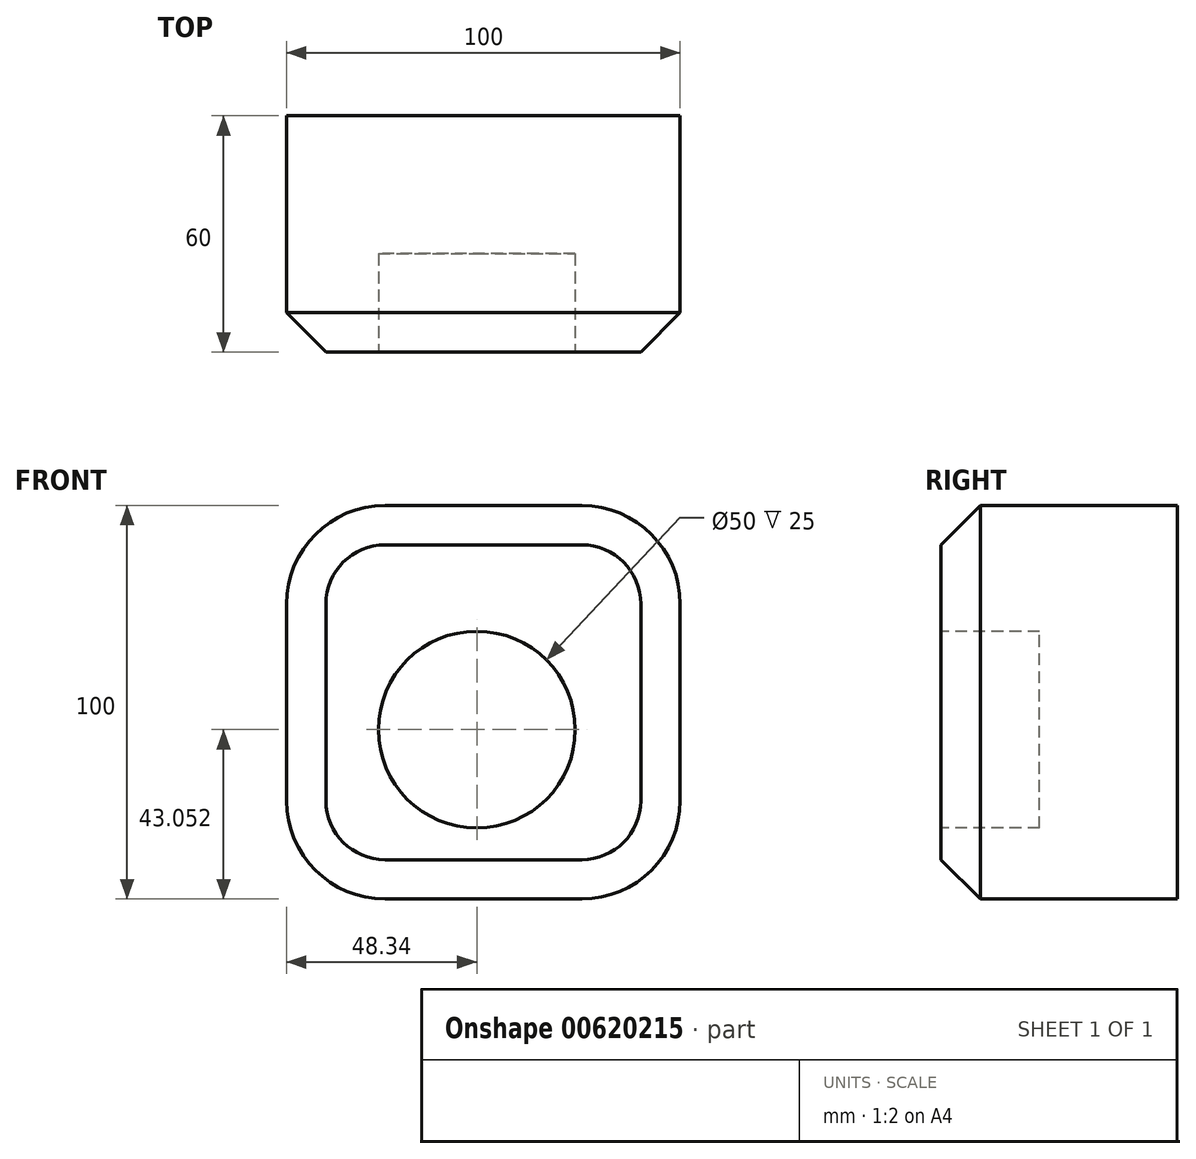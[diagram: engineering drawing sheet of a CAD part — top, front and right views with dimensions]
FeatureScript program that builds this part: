
annotation { "Feature Type Name" : "Feature", "Feature Type Description" : "" }
export const myFeature = defineFeature(function(context is Context, id is Id, definition is map)
    precondition{}
    {
        {
            var Q0;
            Q0=qCreatedBy(makeId("Front.planeOp"),FACE);
            var sketch = newSketch(context, id + "F0", { "sketchPlane" : qUnion([Q0])});
            skLineSegment(sketch, "E0.bottom", {"start": v(-23.34, 80.26) * mm, "end": v(26.66, 80.26) * mm});
            skLineSegment(sketch, "E0.top", {"start": v(-23.34, -19.74) * mm, "end": v(26.66, -19.74) * mm});
            skLineSegment(sketch, "E0.left", {"start": v(-48.34, 55.26) * mm, "end": v(-48.34, 5.26) * mm});
            skLineSegment(sketch, "E0.right", {"start": v(51.66, 55.26) * mm, "end": v(51.66, 5.26) * mm});
            skPoint(sketch, "E1.visualSharp", {"position": v(-48.34, 80.26) * mm});
            skArc(sketch, "E1.filletArc", {"start": v(-23.34, 80.26) * mm, "mid": v(-41.02, 72.94) * mm, "end": v(-48.34, 55.26) * mm});
            skPoint(sketch, "E2.visualSharp", {"position": v(51.66, -19.74) * mm});
            skArc(sketch, "E2.filletArc", {"start": v(26.66, -19.74) * mm, "mid": v(44.34, -12.41) * mm, "end": v(51.66, 5.26) * mm});
            skPoint(sketch, "E3.visualSharp", {"position": v(51.66, 80.26) * mm});
            skArc(sketch, "E3.filletArc", {"start": v(51.66, 55.26) * mm, "mid": v(44.34, 72.94) * mm, "end": v(26.66, 80.26) * mm});
            skPoint(sketch, "E4.visualSharp", {"position": v(-48.34, -19.74) * mm});
            skArc(sketch, "E4.filletArc", {"start": v(-48.34, 5.26) * mm, "mid": v(-41.02, -12.41) * mm, "end": v(-23.34, -19.74) * mm});
            skSolve(sketch);
        }
        {
            var Q0;
            Q0 = qSketchRegion(id + "F0", true);
            extrude(context, id + "F1", {"entities" : qUnion([Q0]), "depth" : 60 * mm, "offsetDistance" : 25 * mm});
        }
        {
            var Q0;
            Q0=makeQuery(id+"F1.opExtrude","CAP_FACE",FACE,{"disambiguationData":[OSD([sQuery(id+"F0.wireOp",EDGE,"E0.bottom"),sQuery(id+"F0.wireOp",EDGE,"E0.top"),sQuery(id+"F0.wireOp",EDGE,"E0.left"),sQuery(id+"F0.wireOp",EDGE,"E0.right"),sQuery(id+"F0.wireOp",EDGE,"E1.filletArc"),sQuery(id+"F0.wireOp",EDGE,"E2.filletArc"),sQuery(id+"F0.wireOp",EDGE,"E3.filletArc"),sQuery(id+"F0.wireOp",EDGE,"E4.filletArc")])],"isStart":false});
            chamfer(context, id + "F2", {"entities" : qUnion([Q0]), "width" : 10 * mm, "tangentPropagation" : true});
        }
        {
            var Q0;
            Q0=makeQuery(id+"F1.opExtrude","CAP_FACE",FACE,{"disambiguationData":[OSD([sQuery(id+"F0.wireOp",EDGE,"E0.bottom"),sQuery(id+"F0.wireOp",EDGE,"E0.top"),sQuery(id+"F0.wireOp",EDGE,"E0.left"),sQuery(id+"F0.wireOp",EDGE,"E0.right"),sQuery(id+"F0.wireOp",EDGE,"E1.filletArc"),sQuery(id+"F0.wireOp",EDGE,"E2.filletArc"),sQuery(id+"F0.wireOp",EDGE,"E3.filletArc"),sQuery(id+"F0.wireOp",EDGE,"E4.filletArc")])],"isStart":false});
            var sketch = newSketch(context, id + "F3", { "sketchPlane" : qUnion([Q0])});
            skCircle(sketch, "E5", {"center": v(0, 23.31) * mm, "radius": 25 * mm});
            skSolve(sketch);
        }
        {
            var Q0;
            Q0 = qSketchRegion(id + "F3", true);
            extrude(context, id + "F4", {"entities" : qUnion([Q0]), "operationType" : NewBodyOperationType.REMOVE, "oppositeDirection" : true, "depth" : 25 * mm, "offsetDistance" : 25 * mm});
        }
    });
